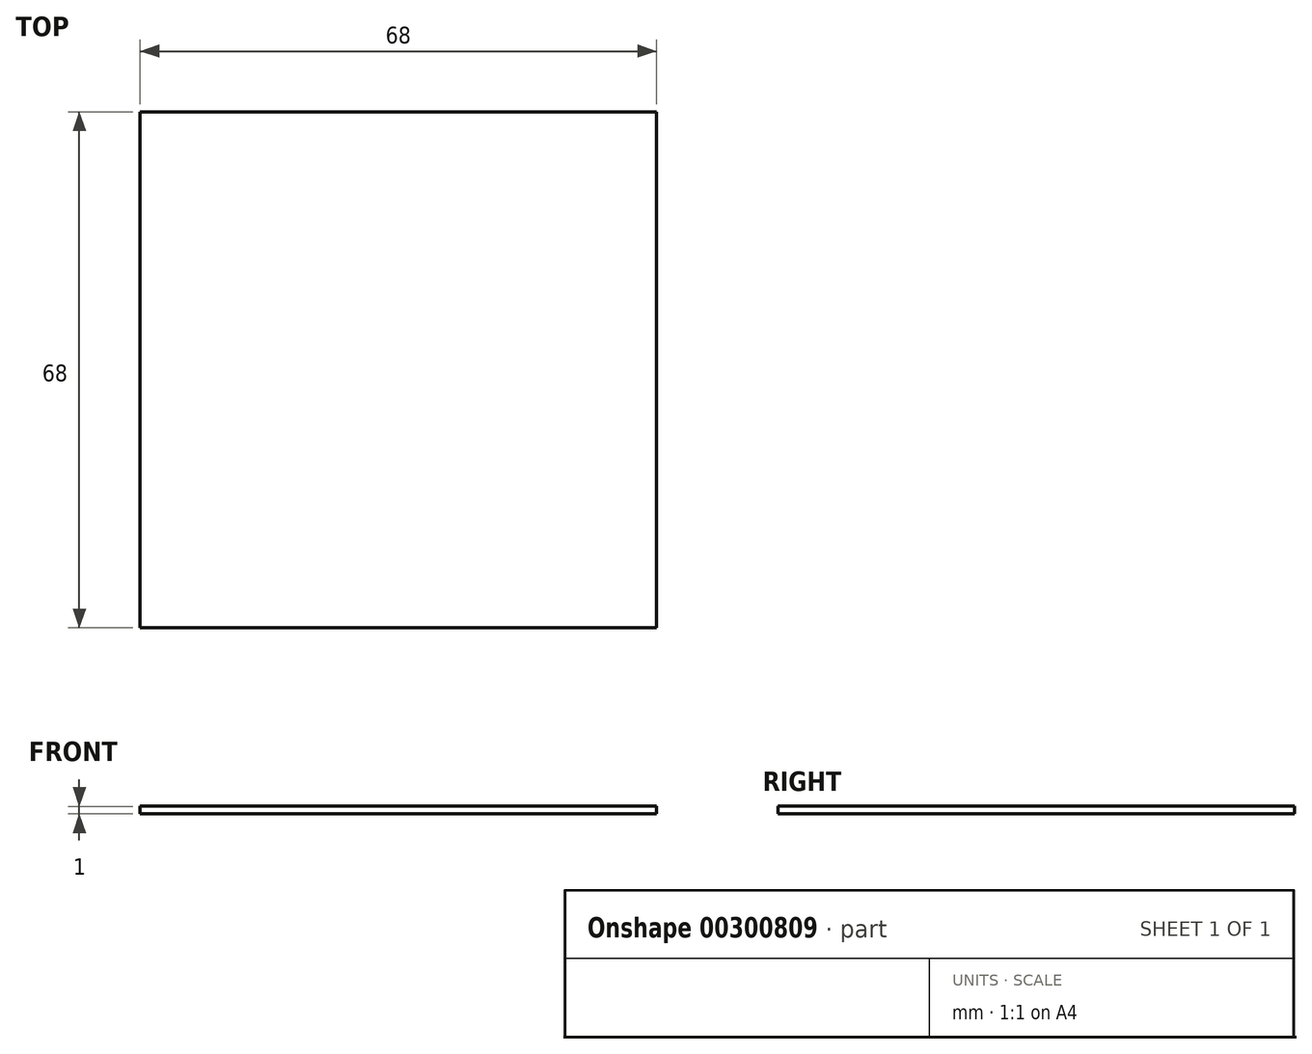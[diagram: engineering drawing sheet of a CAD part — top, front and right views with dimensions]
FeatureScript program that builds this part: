
annotation { "Feature Type Name" : "Feature", "Feature Type Description" : "" }
export const myFeature = defineFeature(function(context is Context, id is Id, definition is map)
    precondition{}
    {
        {
            var Q0;
            Q0=qCreatedBy(makeId("Front.planeOp"),FACE);
            var sketch = newSketch(context, id + "F0", { "sketchPlane" : qUnion([Q0])});
            skLineSegment(sketch, "E0.bottom", {"start": v(-340.86, -144.66) * mm, "end": v(339.14, -144.66) * mm});
            skLineSegment(sketch, "E0.top", {"start": v(-340.86, -154.66) * mm, "end": v(339.14, -154.66) * mm});
            skLineSegment(sketch, "E0.left", {"start": v(-340.86, -144.66) * mm, "end": v(-340.86, -154.66) * mm});
            skLineSegment(sketch, "E0.right", {"start": v(339.14, -144.66) * mm, "end": v(339.14, -154.66) * mm});
            skSolve(sketch);
        }
        {
            var Q0;
            Q0=qSketchRegion(id+"F0",true);
            extrude(context, id + "F1", {"entities" : qUnion([Q0]), "depth" : 680 * mm});
        }
        {
            var Q0;
            Q0=makeQuery(id+"F1.opExtrude","SWEPT_BODY",BODY,{"disambiguationData":[OSD([sQuery(id+"F0.wireOp",EDGE,"E0.bottom"),sQuery(id+"F0.wireOp",EDGE,"E0.top"),sQuery(id+"F0.wireOp",EDGE,"E0.left"),sQuery(id+"F0.wireOp",EDGE,"E0.right")])]});
            var Q1;
            Q1=qCreatedBy(makeId("Origin.pointOp"),VERTEX);
            transform(context, id + "F2", {"entities" : qUnion([Q0]), "transformType" : TransformType.SCALE_UNIFORMLY, "scale" : 0.1, "scalePoint" : qUnion([Q1]), "makeCopy" : false});
        }
    });
